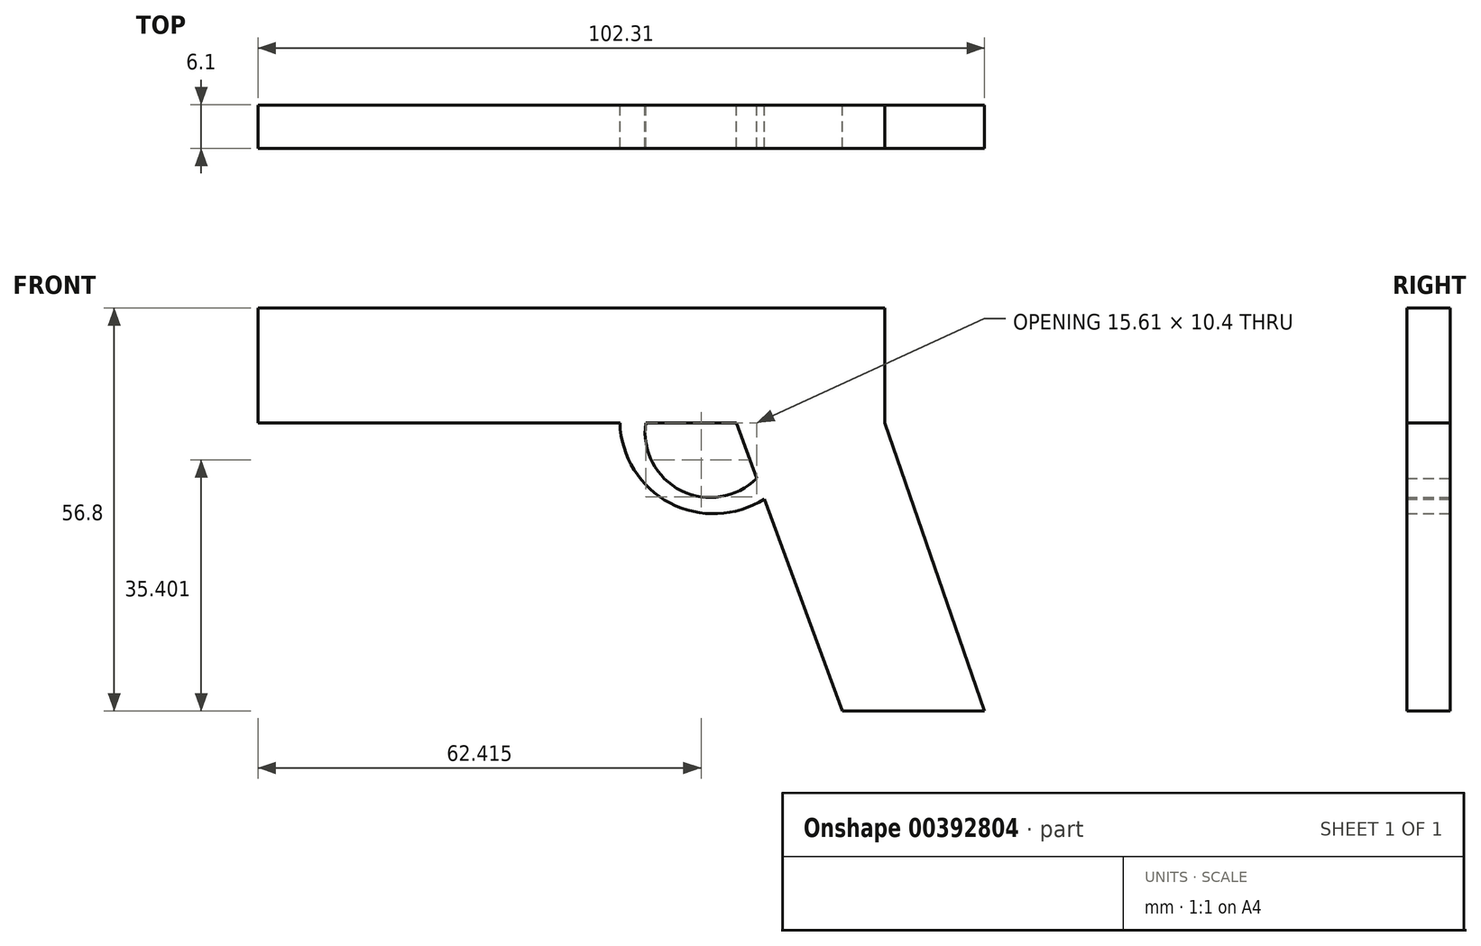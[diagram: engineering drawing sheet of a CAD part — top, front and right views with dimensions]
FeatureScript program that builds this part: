
annotation { "Feature Type Name" : "Feature", "Feature Type Description" : "" }
export const myFeature = defineFeature(function(context is Context, id is Id, definition is map)
    precondition{}
    {
        {
            var Q0;
            Q0=qCreatedBy(makeId("Front.planeOp"),FACE);
            var sketch = newSketch(context, id + "F0", { "sketchPlane" : qUnion([Q0])});
            skLineSegment(sketch, "E0.bottom", {"start": v(-54.61, 60.71) * mm, "end": v(33.68, 60.71) * mm});
            skLineSegment(sketch, "E0.top", {"start": v(-54.61, 44.51) * mm, "end": v(33.68, 44.51) * mm});
            skLineSegment(sketch, "E0.left", {"start": v(-54.61, 60.71) * mm, "end": v(-54.61, 44.51) * mm});
            skLineSegment(sketch, "E0.right", {"start": v(33.68, 60.71) * mm, "end": v(33.68, 44.51) * mm});
            skLineSegment(sketch, "E1", {"start": v(33.68, 44.51) * mm, "end": v(47.7, 3.91) * mm});
            skLineSegment(sketch, "E2", {"start": v(47.7, 3.91) * mm, "end": v(27.67, 3.91) * mm});
            skLineSegment(sketch, "E3", {"start": v(27.67, 3.91) * mm, "end": v(12.74, 44.51) * mm});
            skArc(sketch, "E4", {"start": v(-3.64, 44.51) * mm, "mid": v(3.4, 33.24) * mm, "end": v(16.68, 33.8) * mm});
            skArc(sketch, "E5", {"start": v(0, 44.51) * mm, "mid": v(4.99, 34.98) * mm, "end": v(15.61, 36.71) * mm});
            skSolve(sketch);
        }
        {
            var Q0;
            Q0=makeQuery(id+"F0.imprint","IMPRINT",FACE,{"disambiguationData":[TD([[makeQuery(id+"F0.imprint","IMPRINT",EDGE,{"derivedFrom":sQuery(id+"F0.wireOp",EDGE,"E0.bottom")}),-1.0]])]});
            var Q1;
            {var subQ1=sQuery(id+"F0.wireOp",EDGE,"E1");Q1=makeQuery(id+"F0.imprint","IMPRINT",FACE,{"disambiguationData":[TD([[makeQuery(id+"F0.imprint","IMPRINT",EDGE,{"derivedFrom":subQ1}),-1.0]])]});}
            var Q2;
            {var subQ0=sQuery(id+"F0.wireOp",EDGE,"E4");Q2=makeQuery(id+"F0.imprint","IMPRINT",FACE,{"disambiguationData":[TD([[makeQuery(id+"F0.imprint","IMPRINT",EDGE,{"derivedFrom":subQ0}),1.0]])]});}
            extrude(context, id + "F1", {"entities" : qUnion([Q0, Q1, Q2]), "depth" : 6.1 * mm, "symmetric" : true});
        }
    });
